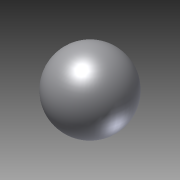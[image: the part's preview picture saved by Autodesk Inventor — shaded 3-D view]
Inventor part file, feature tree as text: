
AUTODESK INVENTOR PART (.ipt)
format: ipt  version: 2013 SP2 (Build 170200200, 200)  size: 114,688 bytes
history: native  units: mm
features: other x7, revolve x1, sketch x1
ambient origin geometry x8: Origin, YZ Plane, XZ Plane, XY Plane, X Axis, Y Axis, Z Axis, Center Point
bodies: Solid1 (feature_tree)
feature tree (9):
  revolve  "Revolution1"  [1 undecoded]
  other  "ball_XY"
  other  "ball_YZ"
  other  "ball_ZX"
  other  "ball_X"
  other  "ball_Y"
  other  "ball_Z"
  other  "ball_Center"
  sketch  "Sketch_1"  dims[d0=360.0deg]
note: 1 required parameter value undecoded (feature->parameter linkage not recoverable at this tier; creation-order binding heuristic only, values carry confidence <= 0.55)
